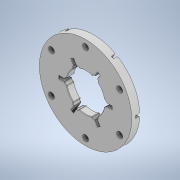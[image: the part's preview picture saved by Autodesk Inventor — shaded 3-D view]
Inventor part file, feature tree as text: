
AUTODESK INVENTOR PART (.ipt)
format: ipt  version: 2020 (Build 240168000, 168)  size: 8,473,600 bytes
history: native  units: in
note: dims shown in document units (in); Inventor stores cm internally (conversion verified against a paired STEP export)
features: projected_geometry x6, extrude x4, sketch x4, other x3, imported_body x1, boolean_combine x1, chamfer x1, reference x1
ambient origin geometry x8: Origin, YZ Plane, XZ Plane, XY Plane, X Axis, Y Axis, Z Axis, Center Point
bodies: Solid1 (feature_tree), Solid2 (feature_tree)
feature tree (21):
  extrude  "Extrusion1"  Depth=0.479in TaperAngle=0.0deg
  imported_body  "Base1"
  boolean_combine  "Combine1"
  extrude  "Extrusion2"  Depth=0.2656in
  extrude  "Extrusion3"  Depth=2.0625in TaperAngle=360.0deg
  chamfer  "Chamfer1"  [1 undecoded]
  extrude  "Extrusion4"  Depth=0.125in TaperAngle=0.0deg
  sketch  "Sketch1"  dims[d0=0.1in d1=0.479in d2=0.0in]
  reference  "Reference1"
  sketch  "Sketch2"  dims[d4=0.0in d5=0.0in d6=0.2656in]
  sketch  "Sketch3"  dims[d7=2.0625in d8=2.3622in d10=360.0deg d12=0.0in d13=0.0in]
  sketch  "Sketch4"  dims[d14=0.025in d15=0.125in d16=45.0deg d17=0.0118in d18=0.0in d19=4.8262in]
  projected_geometry  "Projected Loop1"
  projected_geometry  "Projected Loop2"
  projected_geometry  "Projected Loop3"
  projected_geometry  "Projected Loop4"
  projected_geometry  "Projected Loop5"
  projected_geometry  "Projected Loop6"
  other  "<userpath>\Documents\FRC\2020\Shooter\WheelAndFlywheel.iam"
  other  "WheelAndFlywheel.iam"
  other  "6in 2008 FIRST Hub:1"
note: 1 required parameter value undecoded (feature->parameter linkage not recoverable at this tier; creation-order binding heuristic only, values carry confidence <= 0.55)
